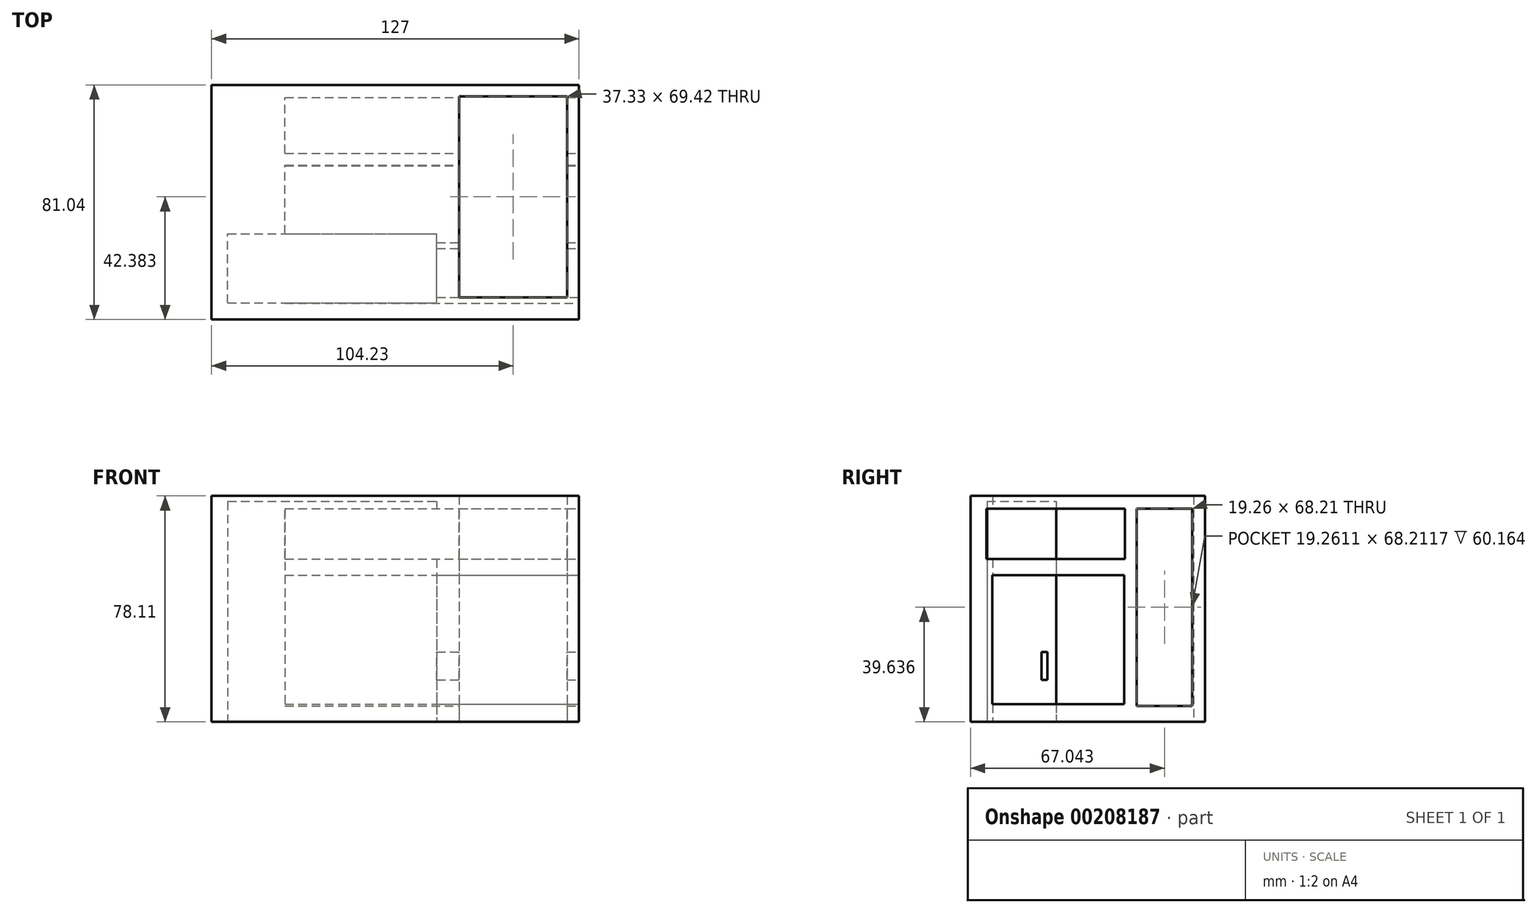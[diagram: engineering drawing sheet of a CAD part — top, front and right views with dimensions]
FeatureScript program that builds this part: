
annotation { "Feature Type Name" : "Feature", "Feature Type Description" : "" }
export const myFeature = defineFeature(function(context is Context, id is Id, definition is map)
    precondition{}
    {
        {
            var Q0;
            Q0=qCreatedBy(makeId("Right.planeOp"),FACE);
            var sketch = newSketch(context, id + "F0", { "sketchPlane" : qUnion([Q0])});
            skLineSegment(sketch, "E0.bottom", {"start": v(-40.52, -34.83) * mm, "end": v(40.52, -34.83) * mm});
            skLineSegment(sketch, "E0.top", {"start": v(-40.52, 43.28) * mm, "end": v(40.52, 43.28) * mm});
            skLineSegment(sketch, "E0.left", {"start": v(-40.52, -34.83) * mm, "end": v(-40.52, 43.28) * mm});
            skLineSegment(sketch, "E0.right", {"start": v(40.52, -34.83) * mm, "end": v(40.52, 43.28) * mm});
            skPoint(sketch, "E0.middle", {"position": v(0, 4.23) * mm});
            skSolve(sketch);
        }
        {
            var Q0;
            Q0=makeQuery(id+"F0.imprint","IMPRINT",FACE,{"disambiguationData":[TD([[makeQuery(id+"F0.imprint","IMPRINT",EDGE,{"derivedFrom":sQuery(id+"F0.wireOp",EDGE,"E0.bottom")}),1.0]])]});
            extrude(context, id + "F1", {"entities" : qUnion([Q0]), "depth" : 127 * mm});
        }
        {
            var Q0;
            Q0=makeQuery(id+"F1.opExtrude","CAP_FACE",FACE,{"disambiguationData":[OSD([sQuery(id+"F0.wireOp",EDGE,"E0.bottom"),sQuery(id+"F0.wireOp",EDGE,"E0.top"),sQuery(id+"F0.wireOp",EDGE,"E0.left"),sQuery(id+"F0.wireOp",EDGE,"E0.right")])],"isStart":false});
            var sketch = newSketch(context, id + "F2", { "sketchPlane" : qUnion([Q0])});
            skLineSegment(sketch, "E1.bottom", {"start": v(-34.98, 21.42) * mm, "end": v(12.82, 21.42) * mm});
            skLineSegment(sketch, "E1.top", {"start": v(-34.98, 38.91) * mm, "end": v(12.82, 38.91) * mm});
            skLineSegment(sketch, "E1.left", {"start": v(-34.98, 21.42) * mm, "end": v(-34.98, 38.91) * mm});
            skLineSegment(sketch, "E1.right", {"start": v(12.82, 21.42) * mm, "end": v(12.82, 38.91) * mm});
            skPoint(sketch, "E1.middle", {"position": v(-11.08, 30.17) * mm});
            skLineSegment(sketch, "E2.bottom", {"start": v(-34.98, -2.19) * mm, "end": v(-7, -2.19) * mm});
            skLineSegment(sketch, "E2.top", {"start": v(-34.98, 17.05) * mm, "end": v(-7, 17.05) * mm});
            skLineSegment(sketch, "E2.left", {"start": v(-34.98, -2.19) * mm, "end": v(-34.98, 17.05) * mm});
            skLineSegment(sketch, "E2.right", {"start": v(-7, -2.19) * mm, "end": v(-7, 17.05) * mm});
            skPoint(sketch, "E2.middle", {"position": v(-20.99, 7.43) * mm});
            skLineSegment(sketch, "E3.bottom", {"start": v(-35.56, -31.63) * mm, "end": v(36.43, -31.63) * mm});
            skLineSegment(sketch, "E3.top", {"start": v(-35.56, -3.35) * mm, "end": v(36.43, -3.35) * mm});
            skLineSegment(sketch, "E3.left", {"start": v(-35.56, -31.63) * mm, "end": v(-35.56, -3.35) * mm});
            skLineSegment(sketch, "E3.right", {"start": v(36.43, -31.63) * mm, "end": v(36.43, -3.35) * mm});
            skLineSegment(sketch, "E4.bottom", {"start": v(16.03, 39.2) * mm, "end": v(36.43, 39.2) * mm});
            skLineSegment(sketch, "E4.top", {"start": v(16.03, 0) * mm, "end": v(36.43, 0) * mm});
            skLineSegment(sketch, "E4.left", {"start": v(16.03, 39.2) * mm, "end": v(16.03, 0) * mm});
            skLineSegment(sketch, "E4.right", {"start": v(36.43, 39.2) * mm, "end": v(36.43, 0) * mm});
            skPoint(sketch, "E5.firstSnap0", {"position": v(16.03, 19.6) * mm});
            skLineSegment(sketch, "E5.bottom", {"start": v(-3.2, 19.6) * mm, "end": v(12.53, 19.6) * mm});
            skLineSegment(sketch, "E5.top", {"start": v(-3.2, 0) * mm, "end": v(12.53, 0) * mm});
            skLineSegment(sketch, "E5.left", {"start": v(-3.2, 19.6) * mm, "end": v(-3.2, 0) * mm});
            skLineSegment(sketch, "E5.right", {"start": v(12.53, 19.6) * mm, "end": v(12.53, 0) * mm});
            skSolve(sketch);
        }
        {
            var Q0;
            Q0=makeQuery(id+"F2.imprint","IMPRINT",FACE,{"disambiguationData":[TD([[makeQuery(id+"F2.imprint","IMPRINT",EDGE,{"derivedFrom":sQuery(id+"F2.wireOp",EDGE,"E1.bottom")}),1.0]])]});
            extrude(context, id + "F3", {"entities" : qUnion([Q0]), "operationType" : NewBodyOperationType.REMOVE, "oppositeDirection" : true, "depth" : 101.6 * mm});
        }
        {
            var Q0;
            Q0=makeQuery(id+"F1.opExtrude","CAP_FACE",FACE,{"disambiguationData":[OSD([sQuery(id+"F0.wireOp",EDGE,"E0.bottom"),sQuery(id+"F0.wireOp",EDGE,"E0.top"),sQuery(id+"F0.wireOp",EDGE,"E0.left"),sQuery(id+"F0.wireOp",EDGE,"E0.right")])],"isStart":false});
            var sketch = newSketch(context, id + "F4", { "sketchPlane" : qUnion([Q0])});
            skLineSegment(sketch, "E6.bottom", {"start": v(-32.95, 15.9) * mm, "end": v(12.54, 15.9) * mm});
            skLineSegment(sketch, "E6.top", {"start": v(-32.95, -28.72) * mm, "end": v(12.54, -28.72) * mm});
            skLineSegment(sketch, "E6.left", {"start": v(-32.95, 15.9) * mm, "end": v(-32.95, -28.72) * mm});
            skLineSegment(sketch, "E6.right", {"start": v(12.54, 15.9) * mm, "end": v(12.54, -28.72) * mm});
            skLineSegment(sketch, "E7.bottom", {"start": v(-16.03, -20.26) * mm, "end": v(-14, -20.26) * mm});
            skLineSegment(sketch, "E7.top", {"start": v(-16.03, -10.64) * mm, "end": v(-14, -10.64) * mm});
            skLineSegment(sketch, "E7.left", {"start": v(-16.03, -20.26) * mm, "end": v(-16.03, -10.64) * mm});
            skLineSegment(sketch, "E7.right", {"start": v(-14, -20.26) * mm, "end": v(-14, -10.64) * mm});
            skSolve(sketch);
        }
        {
            var Q0;
            Q0=makeQuery(id+"F4.imprint","IMPRINT",FACE,{"disambiguationData":[TD([[makeQuery(id+"F4.imprint","IMPRINT",EDGE,{"derivedFrom":sQuery(id+"F4.wireOp",EDGE,"E6.bottom")}),-1.0]])]});
            extrude(context, id + "F5", {"entities" : qUnion([Q0]), "operationType" : NewBodyOperationType.REMOVE, "oppositeDirection" : true, "depth" : 101.6 * mm});
        }
        {
            var Q0;
            {var subQ0=sQuery(id+"F0.wireOp",EDGE,"E0.top");var subQ1=sQuery(id+"F0.wireOp",EDGE,"E0.bottom");var subQ2=sQuery(id+"F0.wireOp",EDGE,"E0.left");var subQ3=sQuery(id+"F0.wireOp",EDGE,"E0.right");Q0=makeQuery(id+"F5.boolean.opBoolean","SPLIT",FACE,{"disambiguationData":[TD([makeQuery(id+"F1.opExtrude","SWEPT_FACE",FACE,{"disambiguationData":[OSD([subQ1])]})])],"derivedFrom":makeQuery(id+"F1.opExtrude","CAP_FACE",FACE,{"disambiguationData":[OSD([subQ1,subQ0,subQ2,subQ3])],"isStart":false})});}
            var sketch = newSketch(context, id + "F6", { "sketchPlane" : qUnion([Q0])});
            skLineSegment(sketch, "E8.bottom", {"start": v(16.9, 38.91) * mm, "end": v(36.15, 38.91) * mm});
            skLineSegment(sketch, "E8.top", {"start": v(16.9, -29.3) * mm, "end": v(36.15, -29.3) * mm});
            skLineSegment(sketch, "E8.left", {"start": v(16.9, 38.91) * mm, "end": v(16.9, -29.3) * mm});
            skLineSegment(sketch, "E8.right", {"start": v(36.15, 38.91) * mm, "end": v(36.15, -29.3) * mm});
            skSolve(sketch);
        }
        {
            var Q0;
            Q0=makeQuery(id+"F6.imprint","IMPRINT",FACE,{"disambiguationData":[TD([[makeQuery(id+"F6.imprint","IMPRINT",EDGE,{"derivedFrom":sQuery(id+"F6.wireOp",EDGE,"E8.bottom")}),-1.0]])]});
            extrude(context, id + "F7", {"entities" : qUnion([Q0]), "operationType" : NewBodyOperationType.REMOVE, "oppositeDirection" : true, "depth" : 101.6 * mm});
        }
        {
            var Q0;
            Q0=makeQuery(id+"F1.opExtrude","SWEPT_FACE",FACE,{"disambiguationData":[OSD([sQuery(id+"F0.wireOp",EDGE,"E0.bottom")])]});
            var sketch = newSketch(context, id + "F8", { "sketchPlane" : qUnion([Q0])});
            skLineSegment(sketch, "E9.bottom", {"start": v(5.58, 34.83) * mm, "end": v(77.87, 34.83) * mm});
            skLineSegment(sketch, "E9.top", {"start": v(5.58, 10.93) * mm, "end": v(77.87, 10.93) * mm});
            skLineSegment(sketch, "E9.left", {"start": v(5.58, 34.83) * mm, "end": v(5.58, 10.93) * mm});
            skLineSegment(sketch, "E9.right", {"start": v(77.87, 34.83) * mm, "end": v(77.87, 10.93) * mm});
            skSolve(sketch);
        }
        {
            var Q0;
            Q0=makeQuery(id+"F8.imprint","IMPRINT",FACE,{"disambiguationData":[TD([[makeQuery(id+"F8.imprint","IMPRINT",EDGE,{"derivedFrom":sQuery(id+"F8.wireOp",EDGE,"E9.bottom")}),-1.0]])]});
            extrude(context, id + "F9", {"entities" : qUnion([Q0]), "operationType" : NewBodyOperationType.REMOVE, "oppositeDirection" : true, "depth" : 76.2 * mm});
        }
        {
            var Q0;
            Q0=makeQuery(id+"F1.opExtrude","SWEPT_FACE",FACE,{"disambiguationData":[OSD([sQuery(id+"F0.wireOp",EDGE,"E0.bottom")])]});
            var sketch = newSketch(context, id + "F10", { "sketchPlane" : qUnion([Q0])});
            skLineSegment(sketch, "E10.bottom", {"start": v(85.56, 32.85) * mm, "end": v(122.9, 32.85) * mm});
            skLineSegment(sketch, "E10.top", {"start": v(85.56, -36.57) * mm, "end": v(122.9, -36.57) * mm});
            skLineSegment(sketch, "E10.left", {"start": v(85.56, 32.85) * mm, "end": v(85.56, -36.57) * mm});
            skLineSegment(sketch, "E10.right", {"start": v(122.9, 32.85) * mm, "end": v(122.9, -36.57) * mm});
            skSolve(sketch);
        }
        {
            var Q0;
            Q0=makeQuery(id+"F10.imprint","IMPRINT",FACE,{"disambiguationData":[TD([[makeQuery(id+"F10.imprint","IMPRINT",EDGE,{"derivedFrom":sQuery(id+"F10.wireOp",EDGE,"E10.bottom")}),-1.0]])]});
            extrude(context, id + "F11", {"entities" : qUnion([Q0]), "operationType" : NewBodyOperationType.REMOVE, "oppositeDirection" : true, "depth" : 101.6 * mm});
        }
    });
